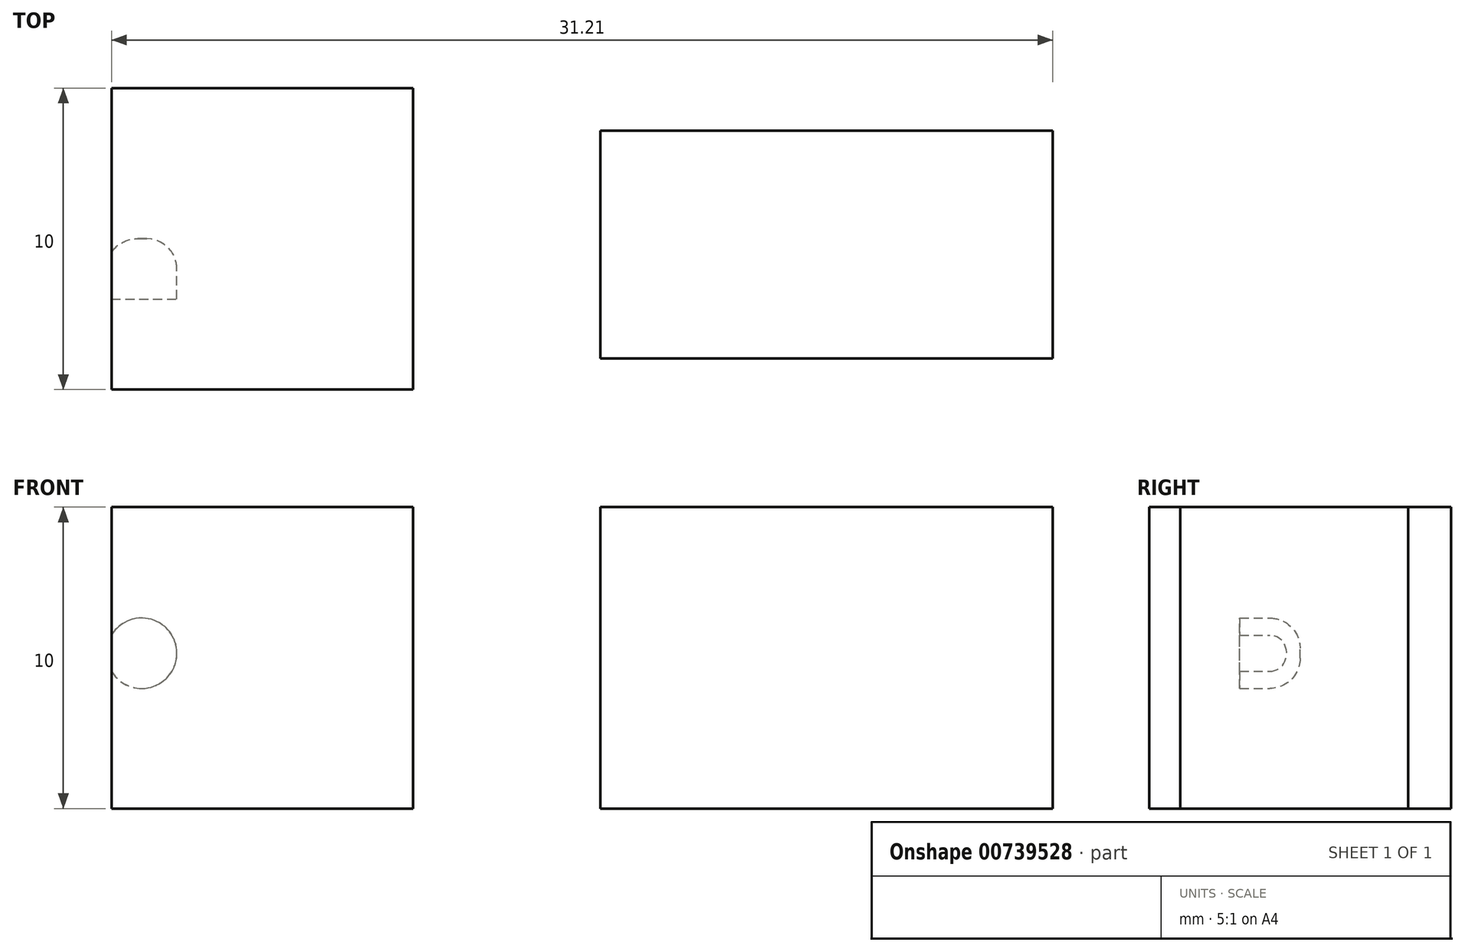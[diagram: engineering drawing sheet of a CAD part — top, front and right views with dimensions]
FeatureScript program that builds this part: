
annotation { "Feature Type Name" : "Feature", "Feature Type Description" : "" }
export const myFeature = defineFeature(function(context is Context, id is Id, definition is map)
    precondition{}
    {
        {
            var Q0;
            Q0=qCreatedBy(makeId("Top.planeOp"),FACE);
            var sketch = newSketch(context, id + "F0", { "sketchPlane" : qUnion([Q0])});
            skLineSegment(sketch, "E0.bottom", {"start": v(5, -5) * mm, "end": v(-5, -5) * mm});
            skLineSegment(sketch, "E0.top", {"start": v(5, 5) * mm, "end": v(-5, 5) * mm});
            skLineSegment(sketch, "E0.left", {"start": v(5, -5) * mm, "end": v(5, 5) * mm});
            skLineSegment(sketch, "E0.right", {"start": v(-5, -5) * mm, "end": v(-5, 5) * mm});
            skPoint(sketch, "E0.middle", {"position": v(0, 0) * mm});
            skPoint(sketch, "E1", {"position": v(0, 2.65) * mm});
            skPoint(sketch, "E2", {"position": v(2.82, 0) * mm});
            skPoint(sketch, "E3", {"position": v(0, -3.96) * mm});
            skLineSegment(sketch, "E4.bottom", {"start": v(11.21, 3.59) * mm, "end": v(26.21, 3.59) * mm});
            skLineSegment(sketch, "E4.top", {"start": v(11.21, -3.97) * mm, "end": v(26.21, -3.97) * mm});
            skLineSegment(sketch, "E4.left", {"start": v(11.21, 3.59) * mm, "end": v(11.21, -3.97) * mm});
            skLineSegment(sketch, "E4.right", {"start": v(26.21, 3.59) * mm, "end": v(26.21, -3.97) * mm});
            skSolve(sketch);
        }
        {
            var Q0;
            Q0=qCreatedBy(makeId("Front.planeOp"),FACE);
            var sketch = newSketch(context, id + "F1", { "sketchPlane" : qUnion([Q0])});
            skCircle(sketch, "E5", {"center": v(-4, 0.15) * mm, "radius": 1.17 * mm});
            skLineSegment(sketch, "E6", {"start": v(-4, 1.42) * mm, "end": v(-4, -0.49) * mm, "construction": true});
            skLineSegment(sketch, "E7", {"start": v(-4.2, 0.15) * mm, "end": v(-1.73, 0.15) * mm, "construction": true});
            skLineSegment(sketch, "E8", {"start": v(0, 1.28) * mm, "end": v(0, -0.72) * mm, "construction": true});
            skLineSegment(sketch, "E9", {"start": v(-3.42, 1.42) * mm, "end": v(-3.42, -1.02) * mm, "construction": true});
            skSolve(sketch);
        }
        {
            var Q0;
            Q0 = qSketchRegion(id + "F0", true);
            var Q1;
            Q1=makeQuery(id+"F0.imprint","IMPRINT",FACE,{"disambiguationData":[TD([[makeQuery(id+"F0.imprint","IMPRINT",EDGE,{"derivedFrom":sQuery(id+"F0.wireOp",EDGE,"E0.bottom")}),-1.0]])]});
            extrude(context, id + "F2", {"entities" : qUnion([Q0, Q1]), "depth" : 10 * mm, "offsetDistance" : 25 * mm, "symmetric" : true});
        }
        {
            var Q0;
            Q0 = qSketchRegion(id + "F1", true);
            extrude(context, id + "F3", {"entities" : qUnion([Q0]), "operationType" : NewBodyOperationType.REMOVE, "depth" : 2 * mm, "offsetDistance" : 25 * mm});
        }
        {
            var Q0;
            Q0=makeQuery(id+"F3.boolean.opBoolean","COPY",EDGE,{"derivedFrom":makeQuery(id+"F3.opExtrude","CAP_EDGE",EDGE,{"disambiguationData":[OSD([sQuery(id+"F1.wireOp",EDGE,"E5")])],"isStart":true})});
            fillet(context, id + "F4", {"entities" : qUnion([Q0]), "radius" : 1 * mm, "tangentPropagation" : true, "allowEdgeOverflow" : false});
        }
    });
